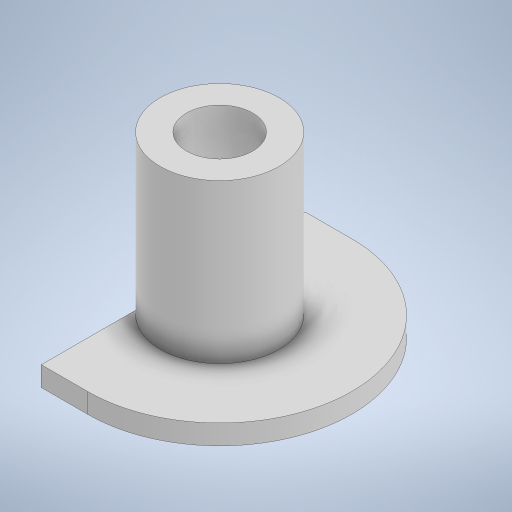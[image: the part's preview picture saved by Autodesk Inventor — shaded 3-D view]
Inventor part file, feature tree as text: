
AUTODESK INVENTOR PART (.ipt)
format: ipt  version: 2024 (Build 280153000, 153)  size: 247,808 bytes
history: native  units: in
note: dims shown in document units (in); Inventor stores cm internally (conversion verified against a paired STEP export)
features: extrude x4, sketch x4
ambient origin geometry x8: Origin, YZ Plane, XZ Plane, XY Plane, X Axis, Y Axis, Z Axis, Center Point
bodies: Solid1 (feature_tree)
feature tree (8):
  extrude  "Extrusion1"  Depth=0.0591in TaperAngle=0.0deg
  extrude  "Extrusion3"  Depth=0.1969in
  extrude  "Extrusion4"  Depth=0.0591in TaperAngle=0.0deg
  extrude  "Extrusion2"  Depth=0.3937in TaperAngle=0.0deg
  sketch  "Sketch1"  dims[d0=0.7874in d1=0.0591in d2=0.0in]
  sketch  "Sketch2"  dims[d3=0.1378in d4=0.1969in]
  sketch  "Sketch3"  dims[d5=0.3543in d6=0.0591in d7=0.0in]
  sketch  "Sketch4"  dims[d8=0.3543in d9=0.3937in d10=0.0591in d11=0.0in d12=0.0in d13=0.1969in d14=0.0787in d15=0.0in d16=0.1181in d17=0.0in d18=0.1969in]
